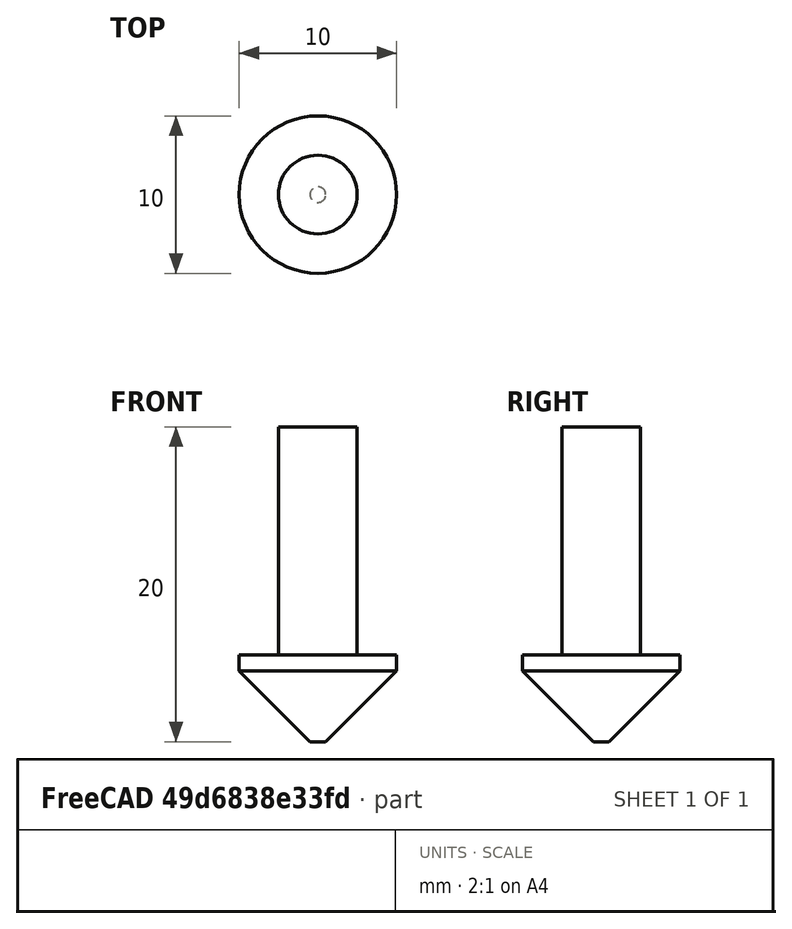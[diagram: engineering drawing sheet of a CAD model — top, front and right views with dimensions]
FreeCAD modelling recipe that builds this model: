
FCSTD DOCUMENT  (FreeCAD 0.19R20874 (Git))
Label: v-bit
License: All rights reserved
LicenseURL: http://en.wikipedia.org/wiki/All_rights_reserved
objects: Sketcher::SketchObject×1, PartDesign::Revolution×1, PartDesign::Body×1
note: 4 computed .brp shape members not serialized (recipe doc carries the construction recipe); baked Part::Feature solids carry a one-line shape summary decoded from their .brp

FEATURE [Sketcher::SketchObject] Sketch
  MapMode = 5
  Placement = pos=(0,0,0) rot=(1,0,0;1.5708rad)
  Support = -> [XZ_Plane]
  sketch-geometry (12):
    g0: LineSegment StartX=-2.1507e-12 StartY=20 StartZ=0 EndX=-2.1507e-12 EndY=-2.0641e-12 EndZ=0
    g1: LineSegment StartX=-2.1507e-12 StartY=-2.0641e-12 StartZ=0 EndX=0.5 EndY=-2.0641e-12 EndZ=0
    g2: LineSegment StartX=0.5 StartY=-2.0641e-12 StartZ=0 EndX=5 EndY=4.5 EndZ=0
    g3: LineSegment StartX=5 StartY=5.5 StartZ=0 EndX=2.5 EndY=5.5 EndZ=0
    g4: LineSegment StartX=2.5 StartY=5.5 StartZ=0 EndX=2.5 EndY=20 EndZ=0
    g5: LineSegment StartX=2.5 StartY=20 StartZ=0 EndX=-2.1507e-12 EndY=20 EndZ=0
    g6: LineSegment [constr] StartX=-5 StartY=4.5 StartZ=0 EndX=5 EndY=4.5 EndZ=0
    g7: LineSegment [constr] StartX=5 StartY=4.5 StartZ=0 EndX=0.5 EndY=-2.0641e-12 EndZ=0
    g8: LineSegment [constr] StartX=0.5 StartY=-2.0641e-12 StartZ=0 EndX=-0.5 EndY=-6.1761e-12 EndZ=0
    g9: LineSegment [constr] StartX=-0.5 StartY=-6.1761e-12 StartZ=0 EndX=-5 EndY=4.5 EndZ=0
    g10: LineSegment [constr] StartX=2.5 StartY=20 StartZ=0 EndX=-2.5 EndY=20 EndZ=0
    g11: LineSegment StartX=5 StartY=4.5 StartZ=0 EndX=5 EndY=5.5 EndZ=0
  constraints (30):
    c: Vertical(g0)
    c: Coincident(g0,g1)
    c: Horizontal(g1)
    c: Coincident(g1,g2)
    c: Horizontal(g3)
    c: Coincident(g3,g4)
    c: Vertical(g4)
    c: Coincident(g4,g5)
    c: Horizontal(g5)
    c: Coincident(g5,g0)
    c: Coincident(g6,g7)
    c: Coincident(g7,g8)
    c: Coincident(g8,g9)
    c: Coincident(g9,g6)
    c: Symmetric(g8,g7,g0)
    c: Coincident(g1,g7)
    c: Coincident(g2,g6)
    c: Symmetric(g2,g6,g0)
    c: DistanceX(g6,g6) = 10  'Diameter; Overall diameter of the V-bit'
    c: Angle(g2,g9) = 1.5708  'CuttingEdgeAngle;Full angle of the v-bit'
    c: DistanceY(g0,g0) = 20  'Length; Overall  bit length'
    c: Coincident(g10,g4)
    c: Symmetric(g10,g4,g-2)
    c: DistanceX(g10,g10) = 5  'ShankDiameter'
    c: Vertical(g11)
    c: Coincident(g3,g11)
    c: Coincident(g11,g2)
    c: DistanceY(g11,g11) = 1  'FlatHeight;Height of the flat extension of the v-bit'
    c: DistanceX(g1) = 0.5  'FlatRadius; Diameter of the flat end of the tip'
    c: Coincident(g-1,g0)
FEATURE [PartDesign::Revolution] Revolution
  AllowMultiFace = false
  Angle = 360
  Axis = (0,-2e-16,1)
  Base = (0,0,0)
  Placement = pos=(0,0,0) rot=(1,0,0;1.5708rad)
  Profile = -> Sketch
  ReferenceAxis = -> Sketch [V_Axis]
  Reversed = true
FEATURE [PartDesign::Body] Body  label="V-Bit"
  Group = -> [Sketch,Revolution]
  Origin = -> Origin
  Tip = -> Revolution
